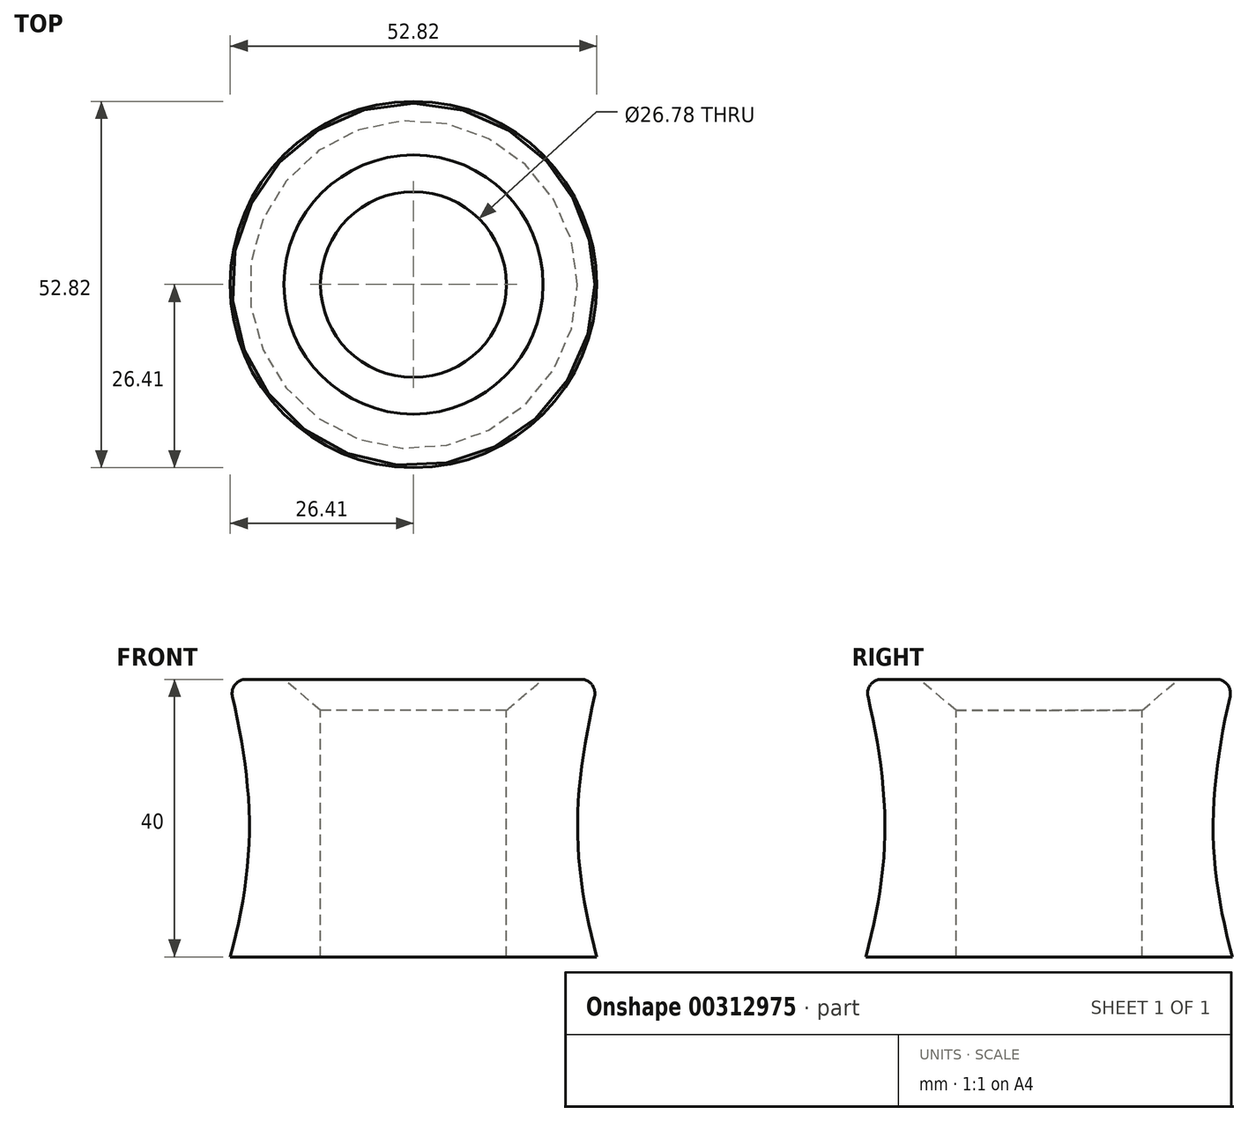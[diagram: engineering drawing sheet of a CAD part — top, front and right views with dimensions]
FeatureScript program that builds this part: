
annotation { "Feature Type Name" : "Feature", "Feature Type Description" : "" }
export const myFeature = defineFeature(function(context is Context, id is Id, definition is map)
    precondition{}
    {
        {
            var Q0;
            Q0=qCreatedBy(makeId("Front.planeOp"),FACE);
            var sketch = newSketch(context, id + "F0", { "sketchPlane" : qUnion([Q0])});
            skLineSegment(sketch, "E0", {"start": v(-13.39, -12.02) * mm, "end": v(-26.41, -12.02) * mm});
            skLineSegment(sketch, "E1", {"start": v(0, 27.98) * mm, "end": v(0, 2.85) * mm});
            skFitSpline(sketch, "E2", {"points": [v(-26.67, 27.98) * mm, v(-23.64, 7.03) * mm, v(-26.41, -12.02) * mm], "startDerivative": vector(10.03, -41.8) * mm, "endDerivative": vector(-10.22, -38.16) * mm});
            skLineSegment(sketch, "E3", {"start": v(-26.67, 27.98) * mm, "end": v(-18.68, 27.98) * mm});
            skLineSegment(sketch, "E4", {"start": v(-18.68, 27.98) * mm, "end": v(-13.39, 23.52) * mm});
            skLineSegment(sketch, "E5", {"start": v(-13.39, 23.52) * mm, "end": v(-13.39, -12.02) * mm});
            skPoint(sketch, "E6", {"position": v(-13.39, 10.85) * mm});
            skSolve(sketch);
        }
        {
            var Q0;
            Q0=makeQuery(id+"F0.imprint","IMPRINT",FACE,{"disambiguationData":[TD([[makeQuery(id+"F0.imprint","IMPRINT",EDGE,{"derivedFrom":sQuery(id+"F0.wireOp",EDGE,"E0")}),-1.0]])]});
            var Q1;
            Q1=sQuery(id+"F0.wireOp",EDGE,"E1");
            revolve(context, id + "F1", {"entities" : qUnion([Q0]), "axis" : qUnion([Q1]), "revolveType" : RevolveType.FULL});
        }
        {
            var Q0;
            Q0=makeQuery(id+"F1.opRevolve","SWEPT_EDGE",EDGE,{"disambiguationData":[OSD([sQuery(id+"F0.wireOp",EDGE,"E2"),sQuery(id+"F0.wireOp",EDGE,"E3")])]});
            fillet(context, id + "F2", {"entities" : qUnion([Q0]), "radius" : 2 * mm, "tangentPropagation" : true, "allowEdgeOverflow" : false});
        }
    });
